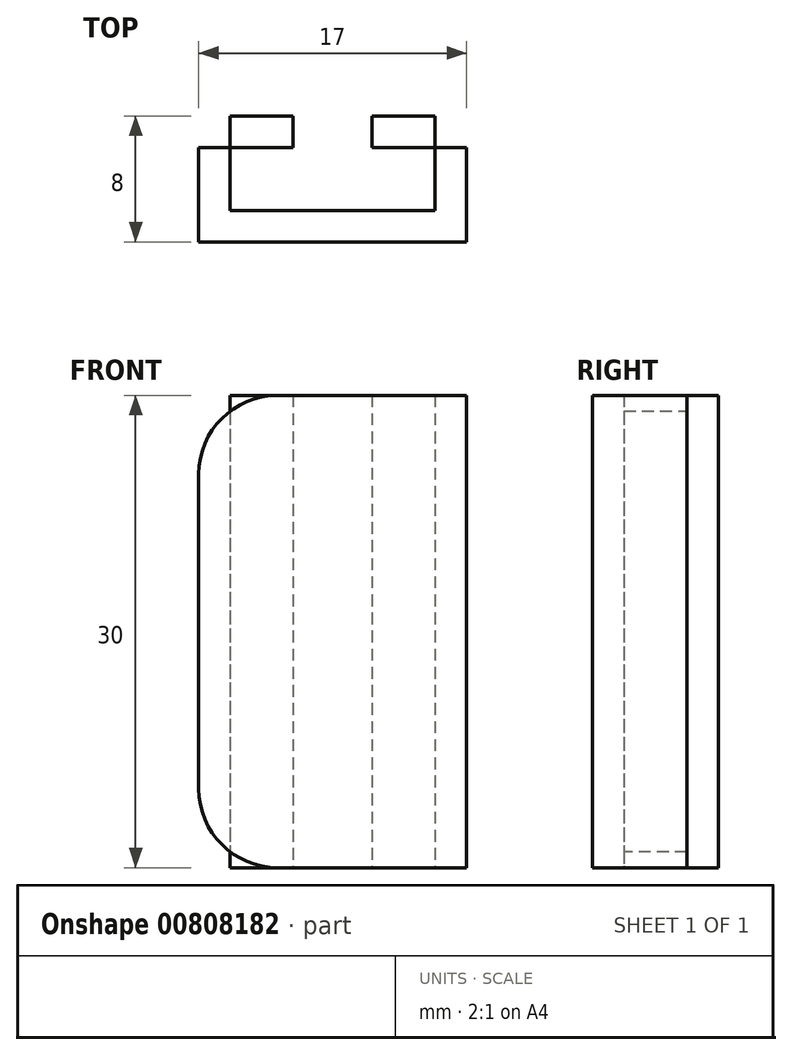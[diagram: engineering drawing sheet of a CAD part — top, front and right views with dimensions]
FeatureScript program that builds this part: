
annotation { "Feature Type Name" : "Feature", "Feature Type Description" : "" }
export const myFeature = defineFeature(function(context is Context, id is Id, definition is map)
    precondition{}
    {
        {
            var Q0;
            Q0=qCreatedBy(makeId("Top.planeOp"),FACE);
            var sketch = newSketch(context, id + "F0", { "sketchPlane" : qUnion([Q0])});
            skLineSegment(sketch, "E0.bottom", {"start": v(0, 0) * mm, "end": v(-8.5, 0) * mm});
            skLineSegment(sketch, "E0.top", {"start": v(0, 2) * mm, "end": v(-8.5, 2) * mm});
            skLineSegment(sketch, "E0.left", {"start": v(0, 0) * mm, "end": v(0, 2) * mm});
            skLineSegment(sketch, "E0.right", {"start": v(-8.5, 0) * mm, "end": v(-8.5, 2) * mm});
            skLineSegment(sketch, "E1.bottom", {"start": v(0, 0) * mm, "end": v(8.5, 0) * mm});
            skLineSegment(sketch, "E1.top", {"start": v(0, 2) * mm, "end": v(8.5, 2) * mm});
            skLineSegment(sketch, "E1.right", {"start": v(8.5, 0) * mm, "end": v(8.5, 2) * mm});
            skLineSegment(sketch, "E2.bottom", {"start": v(-8.5, 0) * mm, "end": v(-6.5, 0) * mm});
            skLineSegment(sketch, "E2.top", {"start": v(-8.5, 8) * mm, "end": v(-6.5, 8) * mm});
            skLineSegment(sketch, "E2.left", {"start": v(-8.5, 0) * mm, "end": v(-8.5, 8) * mm});
            skLineSegment(sketch, "E2.right", {"start": v(-6.5, 0) * mm, "end": v(-6.5, 8) * mm});
            skLineSegment(sketch, "E3.bottom", {"start": v(8.5, 0) * mm, "end": v(6.5, 0) * mm});
            skLineSegment(sketch, "E3.top", {"start": v(8.5, 8) * mm, "end": v(6.5, 8) * mm});
            skLineSegment(sketch, "E3.left", {"start": v(8.5, 0) * mm, "end": v(8.5, 8) * mm});
            skLineSegment(sketch, "E3.right", {"start": v(6.5, 0) * mm, "end": v(6.5, 8) * mm});
            skLineSegment(sketch, "E4.bottom", {"start": v(-8.5, 8) * mm, "end": v(-2.5, 8) * mm});
            skLineSegment(sketch, "E4.top", {"start": v(-8.5, 6) * mm, "end": v(-2.5, 6) * mm});
            skLineSegment(sketch, "E4.left", {"start": v(-8.5, 8) * mm, "end": v(-8.5, 6) * mm});
            skLineSegment(sketch, "E4.right", {"start": v(-2.5, 8) * mm, "end": v(-2.5, 6) * mm});
            skLineSegment(sketch, "E5.bottom", {"start": v(8.5, 8) * mm, "end": v(2.5, 8) * mm});
            skLineSegment(sketch, "E5.top", {"start": v(8.5, 6) * mm, "end": v(2.5, 6) * mm});
            skLineSegment(sketch, "E5.left", {"start": v(8.5, 8) * mm, "end": v(8.5, 6) * mm});
            skLineSegment(sketch, "E5.right", {"start": v(2.5, 8) * mm, "end": v(2.5, 6) * mm});
            skSolve(sketch);
        }
        {
            var Q0;
            {var subQ5=sQuery(id+"F0.wireOp",EDGE,"E4.right");Q0=makeQuery(id+"F0.imprint","IMPRINT",FACE,{"disambiguationData":[TD([[makeQuery(id+"F0.imprint","IMPRINT",EDGE,{"derivedFrom":subQ5}),-1.0]])]});}
            var Q1;
            {var subQ5=sQuery(id+"F0.wireOp",EDGE,"E4.left");Q1=makeQuery(id+"F0.imprint","IMPRINT",FACE,{"disambiguationData":[TD([[makeQuery(id+"F0.imprint","IMPRINT",EDGE,{"derivedFrom":subQ5}),1.0]])]});}
            var Q2;
            {var subQ0=sQuery(id+"F0.wireOp",EDGE,"E2.left");var subQ1=sQuery(id+"F0.wireOp",EDGE,"E0.top");var subQ2=makeQuery(id+"F0.imprint","INTERSECT",VERTEX,{"derivedFrom":[subQ1,subQ0]});Q2=makeQuery(id+"F0.imprint","IMPRINT",FACE,{"disambiguationData":[TD([[makeQuery(id+"F0.imprint","IMPRINT",EDGE,{"disambiguationData":[TD([[subQ2,1.0]])],"derivedFrom":subQ1}),-1.0]])]});}
            var Q3;
            {var subQ5=sQuery(id+"F0.wireOp",EDGE,"E2.bottom");Q3=makeQuery(id+"F0.imprint","IMPRINT",FACE,{"disambiguationData":[TD([[makeQuery(id+"F0.imprint","IMPRINT",EDGE,{"derivedFrom":subQ5}),1.0]])]});}
            var Q4;
            {var subQ0=sQuery(id+"F0.wireOp",EDGE,"E0.bottom");Q4=makeQuery(id+"F0.imprint","IMPRINT",FACE,{"disambiguationData":[TD([[makeQuery(id+"F0.imprint","IMPRINT",EDGE,{"derivedFrom":subQ0}),-1.0]])]});}
            var Q5;
            {var subQ0=sQuery(id+"F0.wireOp",EDGE,"E1.bottom");Q5=makeQuery(id+"F0.imprint","IMPRINT",FACE,{"disambiguationData":[TD([[makeQuery(id+"F0.imprint","IMPRINT",EDGE,{"derivedFrom":subQ0}),1.0]])]});}
            var Q6;
            {var subQ5=sQuery(id+"F0.wireOp",EDGE,"E3.bottom");Q6=makeQuery(id+"F0.imprint","IMPRINT",FACE,{"disambiguationData":[TD([[makeQuery(id+"F0.imprint","IMPRINT",EDGE,{"derivedFrom":subQ5}),-1.0]])]});}
            var Q7;
            {var subQ0=sQuery(id+"F0.wireOp",EDGE,"E3.left");var subQ1=sQuery(id+"F0.wireOp",EDGE,"E1.top");var subQ2=makeQuery(id+"F0.imprint","INTERSECT",VERTEX,{"derivedFrom":[subQ1,subQ0]});Q7=makeQuery(id+"F0.imprint","IMPRINT",FACE,{"disambiguationData":[TD([[makeQuery(id+"F0.imprint","IMPRINT",EDGE,{"disambiguationData":[TD([[subQ2,1.0]])],"derivedFrom":subQ1}),1.0]])]});}
            var Q8;
            {var subQ5=sQuery(id+"F0.wireOp",EDGE,"E5.left");Q8=makeQuery(id+"F0.imprint","IMPRINT",FACE,{"disambiguationData":[TD([[makeQuery(id+"F0.imprint","IMPRINT",EDGE,{"derivedFrom":subQ5}),-1.0]])]});}
            var Q9;
            {var subQ5=sQuery(id+"F0.wireOp",EDGE,"E5.right");Q9=makeQuery(id+"F0.imprint","IMPRINT",FACE,{"disambiguationData":[TD([[makeQuery(id+"F0.imprint","IMPRINT",EDGE,{"derivedFrom":subQ5}),1.0]])]});}
            extrude(context, id + "F1", {"entities" : qUnion([Q0, Q1, Q2, Q3, Q4, Q5, Q6, Q7, Q8, Q9]), "endBound" : BoundingType.SYMMETRIC, "depth" : 30 * mm, "offsetDistance" : 25 * mm});
        }
        {
            var Q0;
            Q0=makeQuery(id+"F1.opExtrude","CAP_EDGE",EDGE,{"disambiguationData":[OSD([sQuery(id+"F0.wireOp",EDGE,"E2.left"),sQuery(id+"F0.wireOp",EDGE,"E4.left")])],"isStart":true});
            var Q1;
            Q1=makeQuery(id+"F1.opExtrude","CAP_EDGE",EDGE,{"disambiguationData":[OSD([sQuery(id+"F0.wireOp",EDGE,"E2.left"),sQuery(id+"F0.wireOp",EDGE,"E4.left")])],"isStart":false});
            fillet(context, id + "F2", {"entities" : qUnion([Q0, Q1]), "radius" : 5 * mm, "tangentPropagation" : true, "allowEdgeOverflow" : false});
        }
    });
